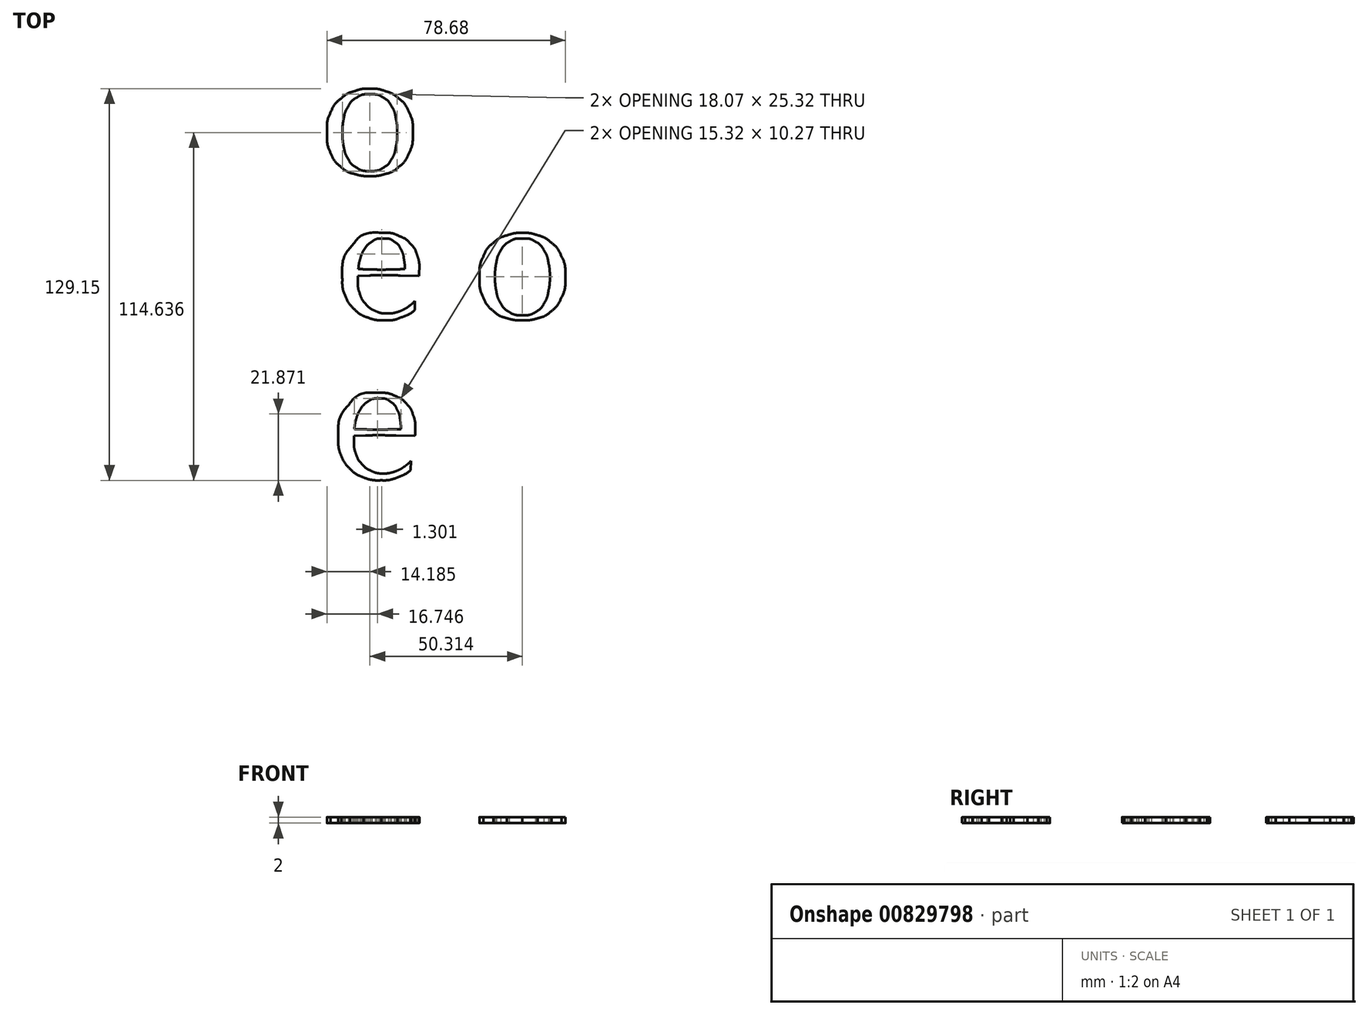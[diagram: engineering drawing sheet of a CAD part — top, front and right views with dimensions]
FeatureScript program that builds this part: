
annotation { "Feature Type Name" : "Feature", "Feature Type Description" : "" }
export const myFeature = defineFeature(function(context is Context, id is Id, definition is map)
    precondition{}
    {
        {
            var Q0;
            Q0=qCreatedBy(makeId("Top.planeOp"),FACE);
            var sketch = newSketch(context, id + "F0", { "sketchPlane" : qUnion([Q0])});
            skLineSegment(sketch, "E0", {"start": v(-57.99, 57.84) * mm, "end": v(-57.99, 47.83) * mm});
            skLineSegment(sketch, "E1", {"start": v(-57.99, 47.83) * mm, "end": v(-57.99, 57.84) * mm});
            skLineSegment(sketch, "E2", {"start": v(-53.21, 47.83) * mm, "end": v(-53.21, 57.84) * mm});
            skLineSegment(sketch, "E3", {"start": v(-53.21, 57.84) * mm, "end": v(-53.21, 47.83) * mm});
            skLineSegment(sketch, "E4", {"start": v(31.74, 55.8) * mm, "end": v(32.14, 56.1) * mm});
            skLineSegment(sketch, "E5", {"start": v(32.14, 56.1) * mm, "end": v(31.74, 55.8) * mm});
            skLineSegment(sketch, "E6", {"start": v(23, 54.88) * mm, "end": v(22.89, 54.93) * mm});
            skLineSegment(sketch, "E7", {"start": v(22.89, 54.93) * mm, "end": v(23, 54.88) * mm});
            skLineSegment(sketch, "E8", {"start": v(18.64, 48.53) * mm, "end": v(18.64, 46.67) * mm});
            skLineSegment(sketch, "E9", {"start": v(18.64, 46.67) * mm, "end": v(18.64, 48.53) * mm});
            skLineSegment(sketch, "E10", {"start": v(22.94, 42.24) * mm, "end": v(22.94, 48.65) * mm});
            skLineSegment(sketch, "E11", {"start": v(22.94, 48.65) * mm, "end": v(22.94, 42.24) * mm});
            skLineSegment(sketch, "E12", {"start": v(56.83, 49.29) * mm, "end": v(56.83, 45.73) * mm});
            skLineSegment(sketch, "E13", {"start": v(56.83, 45.73) * mm, "end": v(56.83, 49.29) * mm});
            skLineSegment(sketch, "E14", {"start": v(61.14, 36.48) * mm, "end": v(61.14, 40.26) * mm});
            skLineSegment(sketch, "E15", {"start": v(61.14, 40.26) * mm, "end": v(61.14, 36.48) * mm});
            skLineSegment(sketch, "E16", {"start": v(42.74, 55.92) * mm, "end": v(42.62, 55.92) * mm});
            skLineSegment(sketch, "E17", {"start": v(42.62, 55.92) * mm, "end": v(42.74, 55.92) * mm});
            skLineSegment(sketch, "E18", {"start": v(38.31, 49.7) * mm, "end": v(38.31, 43.64) * mm});
            skLineSegment(sketch, "E19", {"start": v(38.31, 43.64) * mm, "end": v(38.31, 49.7) * mm});
            skLineSegment(sketch, "E20", {"start": v(42.62, 43.64) * mm, "end": v(42.62, 48.59) * mm});
            skLineSegment(sketch, "E21", {"start": v(42.62, 48.59) * mm, "end": v(42.62, 43.64) * mm});
            skLineSegment(sketch, "E22", {"start": v(-57.28, 2.15) * mm, "end": v(-57.28, -3.9) * mm});
            skLineSegment(sketch, "E23", {"start": v(-57.28, -3.9) * mm, "end": v(-57.28, 2.15) * mm});
            skLineSegment(sketch, "E24", {"start": v(-52.97, -3.9) * mm, "end": v(-52.97, 1.05) * mm});
            skLineSegment(sketch, "E25", {"start": v(-52.97, 1.05) * mm, "end": v(-52.97, -3.9) * mm});
            skLineSegment(sketch, "E26", {"start": v(-35.62, 7.86) * mm, "end": v(-35.74, 7.86) * mm});
            skLineSegment(sketch, "E27", {"start": v(-35.74, 7.86) * mm, "end": v(-35.62, 7.86) * mm});
            skLineSegment(sketch, "E28", {"start": v(-52.86, 8.38) * mm, "end": v(-52.97, 8.38) * mm});
            skLineSegment(sketch, "E29", {"start": v(-52.97, 8.38) * mm, "end": v(-52.86, 8.38) * mm});
            skLineSegment(sketch, "E30", {"start": v(12.53, -11.82) * mm, "end": v(12.88, -8.97) * mm});
            skLineSegment(sketch, "E31", {"start": v(12.88, -8.97) * mm, "end": v(12.59, -8.8) * mm});
            skLineSegment(sketch, "E32", {"start": v(12.59, -8.8) * mm, "end": v(12.53, -11.82) * mm});
            skLineSegment(sketch, "E33", {"start": v(-6.22, -2.16) * mm, "end": v(-6.22, -1.4) * mm});
            skLineSegment(sketch, "E34", {"start": v(-6.22, -1.4) * mm, "end": v(-6.22, -2.16) * mm});
            skLineSegment(sketch, "E35", {"start": v(25.05, 20.84) * mm, "end": v(20.22, 18.8) * mm});
            skLineSegment(sketch, "E36", {"start": v(20.22, 18.8) * mm, "end": v(25.05, 20.84) * mm});
            skLineSegment(sketch, "E37", {"start": v(18.7, 10.07) * mm, "end": v(20.57, 10.07) * mm});
            skLineSegment(sketch, "E38", {"start": v(20.57, 10.07) * mm, "end": v(18.7, 10.07) * mm});
            skLineSegment(sketch, "E39", {"start": v(31.8, -14.5) * mm, "end": v(31.8, -13.1) * mm});
            skLineSegment(sketch, "E40", {"start": v(31.8, -13.1) * mm, "end": v(31.8, -14.5) * mm});
            skLineSegment(sketch, "E41", {"start": v(24.88, 10.07) * mm, "end": v(27.73, 10.07) * mm});
            skLineSegment(sketch, "E42", {"start": v(27.73, 10.07) * mm, "end": v(24.88, 10.07) * mm});
            skLineSegment(sketch, "E43", {"start": v(31, 10.54) * mm, "end": v(31, 11.18) * mm});
            skLineSegment(sketch, "E44", {"start": v(31, 11.18) * mm, "end": v(31, 11.76) * mm});
            skLineSegment(sketch, "E45", {"start": v(31, 11.76) * mm, "end": v(31, 10.54) * mm});
            skLineSegment(sketch, "E46", {"start": v(25.34, 20.84) * mm, "end": v(25.05, 20.84) * mm});
            skLineSegment(sketch, "E47", {"start": v(25.05, 20.84) * mm, "end": v(25.34, 20.84) * mm});
            skLineSegment(sketch, "E48", {"start": v(-22.75, -61.83) * mm, "end": v(-22.93, -67.36) * mm});
            skLineSegment(sketch, "E49", {"start": v(-22.93, -67.36) * mm, "end": v(-22.75, -61.83) * mm});
            skLineSegment(sketch, "E50", {"start": v(-22.93, -39.24) * mm, "end": v(-22.93, -44.95) * mm});
            skLineSegment(sketch, "E51", {"start": v(-22.93, -44.95) * mm, "end": v(-23.05, -44.95) * mm});
            skLineSegment(sketch, "E52", {"start": v(-23.05, -44.95) * mm, "end": v(-22.93, -39.24) * mm});
            skLineSegment(sketch, "E53", {"start": v(-22.87, -61.83) * mm, "end": v(-22.75, -61.83) * mm});
            skLineSegment(sketch, "E54", {"start": v(-22.75, -61.83) * mm, "end": v(-22.87, -61.83) * mm});
            skLineSegment(sketch, "E55", {"start": v(11.23, -64.57) * mm, "end": v(11.58, -61.72) * mm});
            skLineSegment(sketch, "E56", {"start": v(11.58, -61.72) * mm, "end": v(11.29, -61.54) * mm});
            skLineSegment(sketch, "E57", {"start": v(11.29, -61.54) * mm, "end": v(11.23, -64.57) * mm});
            skLineSegment(sketch, "E58", {"start": v(-7.52, -54.9) * mm, "end": v(-7.52, -54.15) * mm});
            skLineSegment(sketch, "E59", {"start": v(-7.52, -54.15) * mm, "end": v(-7.52, -54.9) * mm});
            skLineSegment(sketch, "E60", {"start": v(37.72, -51) * mm, "end": v(37.72, -54.55) * mm});
            skLineSegment(sketch, "E61", {"start": v(37.72, -54.55) * mm, "end": v(37.72, -51) * mm});
            skLineSegment(sketch, "E62", {"start": v(42.03, -63.81) * mm, "end": v(42.03, -60.03) * mm});
            skLineSegment(sketch, "E63", {"start": v(42.03, -60.03) * mm, "end": v(42.03, -63.81) * mm});
            skLineSegment(sketch, "E64", {"start": v(23.63, -44.36) * mm, "end": v(23.52, -44.36) * mm});
            skLineSegment(sketch, "E65", {"start": v(23.52, -44.36) * mm, "end": v(23.63, -44.36) * mm});
            skLineSegment(sketch, "E66", {"start": v(19.2, -50.6) * mm, "end": v(19.2, -56.65) * mm});
            skLineSegment(sketch, "E67", {"start": v(19.2, -56.65) * mm, "end": v(19.2, -50.6) * mm});
            skLineSegment(sketch, "E68", {"start": v(23.52, -56.65) * mm, "end": v(23.52, -51.7) * mm});
            skLineSegment(sketch, "E69", {"start": v(23.52, -51.7) * mm, "end": v(23.52, -56.65) * mm});
            skFitSpline(sketch, "E70", {"points": [v(-57.99, 47.83) * mm, v(-57.99, 45.27) * mm, v(-58.04, 42.75) * mm, v(-58.16, 40.26) * mm]});
            skFitSpline(sketch, "E71", {"points": [v(-58.16, 40.26) * mm, v(-58.24, 37.78) * mm, v(-58.34, 35.33) * mm, v(-58.45, 32.92) * mm]});
            skFitSpline(sketch, "E72", {"points": [v(-58.45, 32.92) * mm, v(-57.13, 33) * mm, v(-55.83, 33.04) * mm, v(-54.55, 33.04) * mm]});
            skFitSpline(sketch, "E73", {"points": [v(-54.55, 33.04) * mm, v(-53.27, 33.04) * mm, v(-51.97, 33.04) * mm, v(-50.65, 33.04) * mm]});
            skFitSpline(sketch, "E74", {"points": [v(-50.65, 33.04) * mm, v(-49.33, 33.04) * mm, v(-48.03, 33.02) * mm, v(-46.75, 32.98) * mm]});
            skFitSpline(sketch, "E75", {"points": [v(-46.75, 32.98) * mm, v(-45.47, 32.94) * mm, v(-44.17, 32.92) * mm, v(-42.85, 32.92) * mm]});
            skFitSpline(sketch, "E76", {"points": [v(-42.85, 32.92) * mm, v(-40.56, 32.92) * mm, v(-38.17, 33.25) * mm, v(-35.69, 33.91) * mm]});
            skFitSpline(sketch, "E77", {"points": [v(-35.69, 33.91) * mm, v(-33.16, 34.61) * mm, v(-30.87, 35.78) * mm, v(-28.82, 37.4) * mm]});
            skFitSpline(sketch, "E78", {"points": [v(-28.82, 37.4) * mm, v(-26.72, 39.04) * mm, v(-25.01, 41.17) * mm, v(-23.7, 43.81) * mm]});
            skFitSpline(sketch, "E79", {"points": [v(-23.7, 43.81) * mm, v(-22.33, 46.5) * mm, v(-21.65, 49.77) * mm, v(-21.65, 53.65) * mm]});
            skFitSpline(sketch, "E80", {"points": [v(-21.65, 53.65) * mm, v(-21.65, 56.64) * mm, v(-22.02, 59.32) * mm, v(-22.76, 61.69) * mm]});
            skFitSpline(sketch, "E81", {"points": [v(-22.76, 61.69) * mm, v(-23.46, 64.1) * mm, v(-24.58, 66.11) * mm, v(-26.14, 67.74) * mm]});
            skFitSpline(sketch, "E82", {"points": [v(-26.14, 67.74) * mm, v(-27.7, 69.41) * mm, v(-29.69, 70.7) * mm, v(-32.13, 71.59) * mm]});
            skFitSpline(sketch, "E83", {"points": [v(-32.13, 71.59) * mm, v(-34.54, 72.48) * mm, v(-37.45, 72.92) * mm, v(-40.87, 72.92) * mm]});
            skFitSpline(sketch, "E84", {"points": [v(-40.87, 72.92) * mm, v(-42.34, 72.92) * mm, v(-43.82, 72.87) * mm, v(-45.3, 72.75) * mm]});
            skFitSpline(sketch, "E85", {"points": [v(-45.3, 72.75) * mm, v(-46.73, 72.67) * mm, v(-48.19, 72.63) * mm, v(-49.66, 72.63) * mm]});
            skFitSpline(sketch, "E86", {"points": [v(-49.66, 72.63) * mm, v(-51.14, 72.63) * mm, v(-52.61, 72.65) * mm, v(-54.09, 72.7) * mm]});
            skFitSpline(sketch, "E87", {"points": [v(-54.09, 72.7) * mm, v(-55.52, 72.77) * mm, v(-56.98, 72.85) * mm, v(-58.45, 72.92) * mm]});
            skFitSpline(sketch, "E88", {"points": [v(-58.45, 72.92) * mm, v(-58.34, 70.36) * mm, v(-58.24, 67.84) * mm, v(-58.16, 65.36) * mm]});
            skFitSpline(sketch, "E89", {"points": [v(-58.16, 65.36) * mm, v(-58.04, 62.91) * mm, v(-57.99, 60.4) * mm, v(-57.99, 57.84) * mm]});
            skFitSpline(sketch, "E90", {"points": [v(-53.21, 57.84) * mm, v(-53.21, 59.94) * mm, v(-53.2, 62) * mm, v(-53.15, 64.02) * mm]});
            skFitSpline(sketch, "E91", {"points": [v(-53.15, 64.02) * mm, v(-53.08, 66.07) * mm, v(-52.98, 68.03) * mm, v(-52.86, 69.9) * mm]});
            skFitSpline(sketch, "E92", {"points": [v(-52.86, 69.9) * mm, v(-51.66, 70.05) * mm, v(-50.3, 70.19) * mm, v(-48.79, 70.3) * mm]});
            skFitSpline(sketch, "E93", {"points": [v(-48.79, 70.3) * mm, v(-47.27, 70.42) * mm, v(-45.64, 70.48) * mm, v(-43.9, 70.48) * mm]});
            skFitSpline(sketch, "E94", {"points": [v(-43.9, 70.48) * mm, v(-41.49, 70.48) * mm, v(-39.28, 70.23) * mm, v(-37.26, 69.72) * mm]});
            skFitSpline(sketch, "E95", {"points": [v(-37.26, 69.72) * mm, v(-35.24, 69.26) * mm, v(-33.51, 68.38) * mm, v(-32.08, 67.1) * mm]});
            skFitSpline(sketch, "E96", {"points": [v(-32.08, 67.1) * mm, v(-30.6, 65.86) * mm, v(-29.46, 64.15) * mm, v(-28.64, 61.98) * mm]});
            skFitSpline(sketch, "E97", {"points": [v(-28.64, 61.98) * mm, v(-27.79, 59.8) * mm, v(-27.36, 57.03) * mm, v(-27.36, 53.65) * mm]});
            skFitSpline(sketch, "E98", {"points": [v(-27.36, 53.65) * mm, v(-27.36, 49.8) * mm, v(-27.9, 46.67) * mm, v(-29, 44.22) * mm]});
            skFitSpline(sketch, "E99", {"points": [v(-29, 44.22) * mm, v(-30.04, 41.81) * mm, v(-31.42, 39.91) * mm, v(-33.12, 38.51) * mm]});
            skFitSpline(sketch, "E100", {"points": [v(-33.12, 38.51) * mm, v(-34.8, 37.12) * mm, v(-36.7, 36.17) * mm, v(-38.83, 35.66) * mm]});
            skFitSpline(sketch, "E101", {"points": [v(-38.83, 35.66) * mm, v(-40.97, 35.16) * mm, v(-43.1, 34.9) * mm, v(-45.24, 34.9) * mm]});
            skFitSpline(sketch, "E102", {"points": [v(-45.24, 34.9) * mm, v(-46.71, 34.9) * mm, v(-48.15, 34.94) * mm, v(-49.54, 35.02) * mm]});
            skFitSpline(sketch, "E103", {"points": [v(-49.54, 35.02) * mm, v(-50.94, 35.14) * mm, v(-52.05, 35.3) * mm, v(-52.86, 35.49) * mm]});
            skFitSpline(sketch, "E104", {"points": [v(-52.86, 35.49) * mm, v(-53.1, 39.52) * mm, v(-53.21, 43.64) * mm, v(-53.21, 47.83) * mm]});
            skFitSpline(sketch, "E105", {"points": [v(-11.27, 46.67) * mm, v(-11.27, 48.3) * mm, v(-11.13, 49.87) * mm, v(-10.86, 51.38) * mm]});
            skFitSpline(sketch, "E106", {"points": [v(-10.86, 51.38) * mm, v(-10.55, 52.9) * mm, v(-10.05, 54.23) * mm, v(-9.35, 55.4) * mm]});
            skFitSpline(sketch, "E107", {"points": [v(-9.35, 55.4) * mm, v(-8.65, 56.6) * mm, v(-7.72, 57.55) * mm, v(-6.55, 58.25) * mm]});
            skFitSpline(sketch, "E108", {"points": [v(-6.55, 58.25) * mm, v(-5.39, 58.95) * mm, v(-3.95, 59.3) * mm, v(-2.25, 59.3) * mm]});
            skFitSpline(sketch, "E109", {"points": [v(-2.25, 59.3) * mm, v(-0.54, 59.3) * mm, v(0.9, 58.95) * mm, v(2.06, 58.25) * mm]});
            skFitSpline(sketch, "E110", {"points": [v(2.06, 58.25) * mm, v(3.23, 57.55) * mm, v(4.16, 56.6) * mm, v(4.86, 55.4) * mm]});
            skFitSpline(sketch, "E111", {"points": [v(4.86, 55.4) * mm, v(5.56, 54.23) * mm, v(6.04, 52.9) * mm, v(6.31, 51.38) * mm]});
            skFitSpline(sketch, "E112", {"points": [v(6.31, 51.38) * mm, v(6.62, 49.87) * mm, v(6.78, 48.3) * mm, v(6.78, 46.67) * mm]});
            skFitSpline(sketch, "E113", {"points": [v(6.78, 46.67) * mm, v(6.78, 45.04) * mm, v(6.62, 43.46) * mm, v(6.31, 41.95) * mm]});
            skFitSpline(sketch, "E114", {"points": [v(6.31, 41.95) * mm, v(6.04, 40.44) * mm, v(5.56, 39.08) * mm, v(4.86, 37.87) * mm]});
            skFitSpline(sketch, "E115", {"points": [v(4.86, 37.87) * mm, v(4.16, 36.7) * mm, v(3.23, 35.78) * mm, v(2.06, 35.08) * mm]});
            skFitSpline(sketch, "E116", {"points": [v(2.06, 35.08) * mm, v(0.9, 34.38) * mm, v(-0.54, 34.03) * mm, v(-2.25, 34.03) * mm]});
            skFitSpline(sketch, "E117", {"points": [v(-2.25, 34.03) * mm, v(-3.95, 34.03) * mm, v(-5.39, 34.38) * mm, v(-6.55, 35.08) * mm]});
            skFitSpline(sketch, "E118", {"points": [v(-6.55, 35.08) * mm, v(-7.72, 35.78) * mm, v(-8.65, 36.7) * mm, v(-9.35, 37.87) * mm]});
            skFitSpline(sketch, "E119", {"points": [v(-9.35, 37.87) * mm, v(-10.05, 39.08) * mm, v(-10.55, 40.44) * mm, v(-10.86, 41.95) * mm]});
            skFitSpline(sketch, "E120", {"points": [v(-10.86, 41.95) * mm, v(-11.13, 43.46) * mm, v(-11.27, 45.04) * mm, v(-11.27, 46.67) * mm]});
            skFitSpline(sketch, "E121", {"points": [v(-16.4, 46.67) * mm, v(-16.4, 44.03) * mm, v(-15.99, 41.77) * mm, v(-15.17, 39.91) * mm]});
            skFitSpline(sketch, "E122", {"points": [v(-15.17, 39.91) * mm, v(-14.32, 38.09) * mm, v(-13.21, 36.6) * mm, v(-11.85, 35.43) * mm]});
            skFitSpline(sketch, "E123", {"points": [v(-11.85, 35.43) * mm, v(-10.5, 34.3) * mm, v(-8.98, 33.5) * mm, v(-7.31, 33.04) * mm]});
            skFitSpline(sketch, "E124", {"points": [v(-7.31, 33.04) * mm, v(-5.6, 32.58) * mm, v(-3.91, 32.34) * mm, v(-2.25, 32.34) * mm]});
            skFitSpline(sketch, "E125", {"points": [v(-2.25, 32.34) * mm, v(-0.54, 32.34) * mm, v(1.15, 32.58) * mm, v(2.82, 33.04) * mm]});
            skFitSpline(sketch, "E126", {"points": [v(2.82, 33.04) * mm, v(4.49, 33.5) * mm, v(6, 34.3) * mm, v(7.36, 35.43) * mm]});
            skFitSpline(sketch, "E127", {"points": [v(7.36, 35.43) * mm, v(8.72, 36.6) * mm, v(9.8, 38.09) * mm, v(10.62, 39.91) * mm]});
            skFitSpline(sketch, "E128", {"points": [v(10.62, 39.91) * mm, v(11.48, 41.77) * mm, v(11.9, 44.03) * mm, v(11.9, 46.67) * mm]});
            skFitSpline(sketch, "E129", {"points": [v(11.9, 46.67) * mm, v(11.9, 49.3) * mm, v(11.48, 51.54) * mm, v(10.62, 53.36) * mm]});
            skFitSpline(sketch, "E130", {"points": [v(10.62, 53.36) * mm, v(9.8, 55.22) * mm, v(8.72, 56.72) * mm, v(7.36, 57.84) * mm]});
            skFitSpline(sketch, "E131", {"points": [v(7.36, 57.84) * mm, v(6, 59) * mm, v(4.49, 59.84) * mm, v(2.82, 60.35) * mm]});
            skFitSpline(sketch, "E132", {"points": [v(2.82, 60.35) * mm, v(1.15, 60.9) * mm, v(-0.54, 61.16) * mm, v(-2.25, 61.16) * mm]});
            skFitSpline(sketch, "E133", {"points": [v(-2.25, 61.16) * mm, v(-3.91, 61.16) * mm, v(-5.6, 60.9) * mm, v(-7.31, 60.35) * mm]});
            skFitSpline(sketch, "E134", {"points": [v(-7.31, 60.35) * mm, v(-8.98, 59.84) * mm, v(-10.5, 59) * mm, v(-11.85, 57.84) * mm]});
            skFitSpline(sketch, "E135", {"points": [v(-11.85, 57.84) * mm, v(-13.21, 56.72) * mm, v(-14.32, 55.22) * mm, v(-15.17, 53.36) * mm]});
            skFitSpline(sketch, "E136", {"points": [v(-15.17, 53.36) * mm, v(-15.99, 51.54) * mm, v(-16.4, 49.3) * mm, v(-16.4, 46.67) * mm]});
            skFitSpline(sketch, "E137", {"points": [v(32.14, 56.1) * mm, v(32.14, 56.87) * mm, v(32.16, 57.73) * mm, v(32.2, 58.66) * mm]});
            skFitSpline(sketch, "E138", {"points": [v(32.2, 58.66) * mm, v(32.24, 59.63) * mm, v(32.36, 60.35) * mm, v(32.55, 60.81) * mm]});
            skFitSpline(sketch, "E139", {"points": [v(32.55, 60.81) * mm, v(32.16, 60.97) * mm, v(31.83, 61.07) * mm, v(31.56, 61.1) * mm]});
            skFitSpline(sketch, "E140", {"points": [v(31.56, 61.1) * mm, v(31.33, 61.14) * mm, v(31.04, 61.16) * mm, v(30.69, 61.16) * mm]});
            skFitSpline(sketch, "E141", {"points": [v(30.69, 61.16) * mm, v(27.85, 61.16) * mm, v(25.3, 59.07) * mm, v(23, 54.88) * mm]});
            skFitSpline(sketch, "E142", {"points": [v(22.89, 54.93) * mm, v(22.89, 55.67) * mm, v(22.89, 56.45) * mm, v(22.89, 57.26) * mm]});
            skFitSpline(sketch, "E143", {"points": [v(22.89, 57.26) * mm, v(22.93, 58.08) * mm, v(23.02, 59.18) * mm, v(23.18, 60.58) * mm]});
            skFitSpline(sketch, "E144", {"points": [v(23.18, 60.58) * mm, v(22.75, 60.5) * mm, v(22.34, 60.43) * mm, v(21.95, 60.35) * mm]});
            skFitSpline(sketch, "E145", {"points": [v(21.95, 60.35) * mm, v(21.57, 60.3) * mm, v(21.2, 60.3) * mm, v(20.85, 60.3) * mm]});
            skFitSpline(sketch, "E146", {"points": [v(20.85, 60.3) * mm, v(20.42, 60.3) * mm, v(20.01, 60.3) * mm, v(19.63, 60.35) * mm]});
            skFitSpline(sketch, "E147", {"points": [v(19.63, 60.35) * mm, v(19.24, 60.43) * mm, v(18.83, 60.5) * mm, v(18.4, 60.58) * mm]});
            skFitSpline(sketch, "E148", {"points": [v(18.4, 60.58) * mm, v(18.52, 58.02) * mm, v(18.58, 55.75) * mm, v(18.58, 53.77) * mm]});
            skFitSpline(sketch, "E149", {"points": [v(18.58, 53.77) * mm, v(18.62, 51.79) * mm, v(18.64, 50.04) * mm, v(18.64, 48.53) * mm]});
            skFitSpline(sketch, "E150", {"points": [v(18.64, 46.67) * mm, v(18.64, 43.37) * mm, v(18.62, 40.57) * mm, v(18.58, 38.28) * mm]});
            skFitSpline(sketch, "E151", {"points": [v(18.58, 38.28) * mm, v(18.58, 36.03) * mm, v(18.52, 34.24) * mm, v(18.4, 32.92) * mm]});
            skFitSpline(sketch, "E152", {"points": [v(18.4, 32.92) * mm, v(19.18, 33) * mm, v(20, 33.04) * mm, v(20.85, 33.04) * mm]});
            skFitSpline(sketch, "E153", {"points": [v(20.85, 33.04) * mm, v(21.62, 33.04) * mm, v(22.4, 33) * mm, v(23.18, 32.92) * mm]});
            skFitSpline(sketch, "E154", {"points": [v(23.18, 32.92) * mm, v(23.06, 33.78) * mm, v(22.98, 34.88) * mm, v(22.94, 36.24) * mm]});
            skFitSpline(sketch, "E155", {"points": [v(22.94, 36.24) * mm, v(22.94, 37.64) * mm, v(22.94, 39.64) * mm, v(22.94, 42.24) * mm]});
            skFitSpline(sketch, "E156", {"points": [v(22.94, 48.65) * mm, v(22.94, 49.77) * mm, v(23.08, 50.82) * mm, v(23.35, 51.79) * mm]});
            skFitSpline(sketch, "E157", {"points": [v(23.35, 51.79) * mm, v(23.62, 52.8) * mm, v(24.01, 53.65) * mm, v(24.52, 54.35) * mm]});
            skFitSpline(sketch, "E158", {"points": [v(24.52, 54.35) * mm, v(25.02, 55.09) * mm, v(25.64, 55.67) * mm, v(26.38, 56.1) * mm]});
            skFitSpline(sketch, "E159", {"points": [v(26.38, 56.1) * mm, v(27.12, 56.52) * mm, v(27.95, 56.74) * mm, v(28.88, 56.74) * mm]});
            skFitSpline(sketch, "E160", {"points": [v(28.88, 56.74) * mm, v(29.47, 56.74) * mm, v(30.03, 56.64) * mm, v(30.57, 56.45) * mm]});
            skFitSpline(sketch, "E161", {"points": [v(30.57, 56.45) * mm, v(31.15, 56.25) * mm, v(31.54, 56.04) * mm, v(31.74, 55.8) * mm]});
            skFitSpline(sketch, "E162", {"points": [v(56.83, 45.73) * mm, v(56.83, 43.48) * mm, v(56.77, 41.29) * mm, v(56.66, 39.15) * mm]});
            skFitSpline(sketch, "E163", {"points": [v(56.66, 39.15) * mm, v(56.58, 37.02) * mm, v(56.5, 34.94) * mm, v(56.42, 32.92) * mm]});
            skFitSpline(sketch, "E164", {"points": [v(56.42, 32.92) * mm, v(57.2, 33) * mm, v(58, 33.04) * mm, v(58.8, 33.04) * mm]});
            skFitSpline(sketch, "E165", {"points": [v(58.8, 33.04) * mm, v(59.66, 33.04) * mm, v(60.48, 33) * mm, v(61.26, 32.92) * mm]});
            skFitSpline(sketch, "E166", {"points": [v(61.26, 32.92) * mm, v(61.22, 33.47) * mm, v(61.18, 34.03) * mm, v(61.14, 34.61) * mm]});
            skFitSpline(sketch, "E167", {"points": [v(61.14, 34.61) * mm, v(61.14, 35.23) * mm, v(61.14, 35.86) * mm, v(61.14, 36.48) * mm]});
            skFitSpline(sketch, "E168", {"points": [v(61.14, 40.26) * mm, v(61.14, 42.24) * mm, v(61.18, 44.1) * mm, v(61.26, 45.85) * mm]});
            skFitSpline(sketch, "E169", {"points": [v(61.26, 45.85) * mm, v(61.33, 47.64) * mm, v(61.37, 49.36) * mm, v(61.37, 51.03) * mm]});
            skFitSpline(sketch, "E170", {"points": [v(61.37, 51.03) * mm, v(61.37, 53.05) * mm, v(61.08, 54.7) * mm, v(60.5, 55.98) * mm]});
            skFitSpline(sketch, "E171", {"points": [v(60.5, 55.98) * mm, v(59.95, 57.3) * mm, v(59.24, 58.33) * mm, v(58.34, 59.07) * mm]});
            skFitSpline(sketch, "E172", {"points": [v(58.34, 59.07) * mm, v(57.45, 59.84) * mm, v(56.44, 60.39) * mm, v(55.32, 60.7) * mm]});
            skFitSpline(sketch, "E173", {"points": [v(55.32, 60.7) * mm, v(54.23, 61) * mm, v(53.14, 61.16) * mm, v(52.06, 61.16) * mm]});
            skFitSpline(sketch, "E174", {"points": [v(52.06, 61.16) * mm, v(49.96, 61.16) * mm, v(48.15, 60.7) * mm, v(46.64, 59.77) * mm]});
            skFitSpline(sketch, "E175", {"points": [v(46.64, 59.77) * mm, v(45.13, 58.87) * mm, v(43.83, 57.6) * mm, v(42.74, 55.92) * mm]});
            skFitSpline(sketch, "E176", {"points": [v(42.62, 55.92) * mm, v(42.62, 57.48) * mm, v(42.68, 59.03) * mm, v(42.8, 60.58) * mm]});
            skFitSpline(sketch, "E177", {"points": [v(42.8, 60.58) * mm, v(42.3, 60.5) * mm, v(41.85, 60.43) * mm, v(41.46, 60.35) * mm]});
            skFitSpline(sketch, "E178", {"points": [v(41.46, 60.35) * mm, v(41.1, 60.3) * mm, v(40.78, 60.3) * mm, v(40.47, 60.3) * mm]});
            skFitSpline(sketch, "E179", {"points": [v(40.47, 60.3) * mm, v(39.8, 60.3) * mm, v(38.94, 60.39) * mm, v(37.85, 60.58) * mm]});
            skFitSpline(sketch, "E180", {"points": [v(37.85, 60.58) * mm, v(38.04, 58.91) * mm, v(38.16, 57.1) * mm, v(38.2, 55.17) * mm]});
            skFitSpline(sketch, "E181", {"points": [v(38.2, 55.17) * mm, v(38.28, 53.26) * mm, v(38.31, 51.44) * mm, v(38.31, 49.7) * mm]});
            skFitSpline(sketch, "E182", {"points": [v(38.31, 43.64) * mm, v(38.31, 41.9) * mm, v(38.28, 40.05) * mm, v(38.2, 38.1) * mm]});
            skFitSpline(sketch, "E183", {"points": [v(38.2, 38.1) * mm, v(38.16, 36.2) * mm, v(38.04, 34.48) * mm, v(37.85, 32.92) * mm]});
            skFitSpline(sketch, "E184", {"points": [v(37.85, 32.92) * mm, v(38.74, 33) * mm, v(39.62, 33.04) * mm, v(40.47, 33.04) * mm]});
            skFitSpline(sketch, "E185", {"points": [v(40.47, 33.04) * mm, v(41.32, 33.04) * mm, v(42.2, 33) * mm, v(43.09, 32.92) * mm]});
            skFitSpline(sketch, "E186", {"points": [v(43.09, 32.92) * mm, v(42.9, 34.48) * mm, v(42.76, 36.2) * mm, v(42.68, 38.1) * mm]});
            skFitSpline(sketch, "E187", {"points": [v(42.68, 38.1) * mm, v(42.64, 40.05) * mm, v(42.62, 41.9) * mm, v(42.62, 43.64) * mm]});
            skFitSpline(sketch, "E188", {"points": [v(42.62, 48.59) * mm, v(42.62, 51.61) * mm, v(43.24, 53.96) * mm, v(44.49, 55.63) * mm]});
            skFitSpline(sketch, "E189", {"points": [v(44.49, 55.63) * mm, v(45.77, 57.3) * mm, v(47.77, 58.14) * mm, v(50.48, 58.14) * mm]});
            skFitSpline(sketch, "E190", {"points": [v(50.48, 58.14) * mm, v(52.46, 58.14) * mm, v(54.02, 57.38) * mm, v(55.14, 55.87) * mm]});
            skFitSpline(sketch, "E191", {"points": [v(55.14, 55.87) * mm, v(56.27, 54.4) * mm, v(56.83, 52.2) * mm, v(56.83, 49.29) * mm]});
            skFitSpline(sketch, "E192", {"points": [v(-57.28, -3.9) * mm, v(-57.28, -5.65) * mm, v(-57.32, -7.5) * mm, v(-57.4, -9.43) * mm]});
            skFitSpline(sketch, "E193", {"points": [v(-57.4, -9.43) * mm, v(-57.44, -11.34) * mm, v(-57.55, -13.06) * mm, v(-57.75, -14.62) * mm]});
            skFitSpline(sketch, "E194", {"points": [v(-57.75, -14.62) * mm, v(-56.85, -14.54) * mm, v(-55.98, -14.5) * mm, v(-55.13, -14.5) * mm]});
            skFitSpline(sketch, "E195", {"points": [v(-55.13, -14.5) * mm, v(-54.27, -14.5) * mm, v(-53.4, -14.54) * mm, v(-52.5, -14.62) * mm]});
            skFitSpline(sketch, "E196", {"points": [v(-52.5, -14.62) * mm, v(-52.7, -13.06) * mm, v(-52.84, -11.34) * mm, v(-52.91, -9.43) * mm]});
            skFitSpline(sketch, "E197", {"points": [v(-52.91, -9.43) * mm, v(-52.95, -7.5) * mm, v(-52.97, -5.65) * mm, v(-52.97, -3.9) * mm]});
            skFitSpline(sketch, "E198", {"points": [v(-52.97, 1.05) * mm, v(-52.97, 4.07) * mm, v(-52.37, 6.42) * mm, v(-51.17, 8.1) * mm]});
            skFitSpline(sketch, "E199", {"points": [v(-51.17, 8.1) * mm, v(-49.96, 9.76) * mm, v(-48.08, 10.6) * mm, v(-45.52, 10.6) * mm]});
            skFitSpline(sketch, "E200", {"points": [v(-45.52, 10.6) * mm, v(-44.55, 10.6) * mm, v(-43.62, 10.32) * mm, v(-42.73, 9.78) * mm]});
            skFitSpline(sketch, "E201", {"points": [v(-42.73, 9.78) * mm, v(-41.8, 9.28) * mm, v(-41.11, 8.65) * mm, v(-40.69, 7.92) * mm]});
            skFitSpline(sketch, "E202", {"points": [v(-40.69, 7.92) * mm, v(-40.45, 7.45) * mm, v(-40.28, 7.02) * mm, v(-40.16, 6.64) * mm]});
            skFitSpline(sketch, "E203", {"points": [v(-40.16, 6.64) * mm, v(-40, 6.25) * mm, v(-39.9, 5.74) * mm, v(-39.81, 5.12) * mm]});
            skFitSpline(sketch, "E204", {"points": [v(-39.81, 5.12) * mm, v(-39.74, 4.54) * mm, v(-39.7, 3.72) * mm, v(-39.7, 2.68) * mm]});
            skFitSpline(sketch, "E205", {"points": [v(-39.7, 2.68) * mm, v(-39.66, 1.67) * mm, v(-39.64, 0.25) * mm, v(-39.64, -1.57) * mm]});
            skFitSpline(sketch, "E206", {"points": [v(-39.64, -1.57) * mm, v(-39.64, -3.7) * mm, v(-39.68, -5.88) * mm, v(-39.76, -8.1) * mm]});
            skFitSpline(sketch, "E207", {"points": [v(-39.76, -8.1) * mm, v(-39.83, -10.3) * mm, v(-39.97, -12.48) * mm, v(-40.16, -14.62) * mm]});
            skFitSpline(sketch, "E208", {"points": [v(-40.16, -14.62) * mm, v(-39.27, -14.54) * mm, v(-38.42, -14.5) * mm, v(-37.6, -14.5) * mm]});
            skFitSpline(sketch, "E209", {"points": [v(-37.6, -14.5) * mm, v(-36.79, -14.5) * mm, v(-35.93, -14.54) * mm, v(-35.04, -14.62) * mm]});
            skFitSpline(sketch, "E210", {"points": [v(-35.04, -14.62) * mm, v(-35.12, -12.99) * mm, v(-35.2, -11.5) * mm, v(-35.27, -10.13) * mm]});
            skFitSpline(sketch, "E211", {"points": [v(-35.27, -10.13) * mm, v(-35.31, -8.74) * mm, v(-35.33, -7.2) * mm, v(-35.33, -5.53) * mm]});
            skFitSpline(sketch, "E212", {"points": [v(-35.33, -5.53) * mm, v(-35.33, -2.78) * mm, v(-35.31, -0.62) * mm, v(-35.27, 0.93) * mm]});
            skFitSpline(sketch, "E213", {"points": [v(-35.27, 0.93) * mm, v(-35.23, 2.52) * mm, v(-35.18, 3.74) * mm, v(-35.1, 4.6) * mm]});
            skFitSpline(sketch, "E214", {"points": [v(-35.1, 4.6) * mm, v(-34.98, 5.5) * mm, v(-34.85, 6.15) * mm, v(-34.7, 6.58) * mm]});
            skFitSpline(sketch, "E215", {"points": [v(-34.7, 6.58) * mm, v(-34.5, 7) * mm, v(-34.24, 7.43) * mm, v(-33.93, 7.86) * mm]});
            skFitSpline(sketch, "E216", {"points": [v(-33.93, 7.86) * mm, v(-33.39, 8.6) * mm, v(-32.63, 9.24) * mm, v(-31.66, 9.78) * mm]});
            skFitSpline(sketch, "E217", {"points": [v(-31.66, 9.78) * mm, v(-30.7, 10.32) * mm, v(-29.5, 10.6) * mm, v(-28.11, 10.6) * mm]});
            skFitSpline(sketch, "E218", {"points": [v(-28.11, 10.6) * mm, v(-26.95, 10.6) * mm, v(-25.98, 10.4) * mm, v(-25.2, 10.01) * mm]});
            skFitSpline(sketch, "E219", {"points": [v(-25.2, 10.01) * mm, v(-24.42, 9.66) * mm, v(-23.8, 9.18) * mm, v(-23.34, 8.56) * mm]});
            skFitSpline(sketch, "E220", {"points": [v(-23.34, 8.56) * mm, v(-22.87, 7.94) * mm, v(-22.54, 7.2) * mm, v(-22.35, 6.34) * mm]});
            skFitSpline(sketch, "E221", {"points": [v(-22.35, 6.34) * mm, v(-22.11, 5.5) * mm, v(-22, 4.58) * mm, v(-22, 3.6) * mm]});
            skFitSpline(sketch, "E222", {"points": [v(-22, 3.6) * mm, v(-22, -1.67) * mm, v(-22.07, -5.79) * mm, v(-22.23, -8.74) * mm]});
            skFitSpline(sketch, "E223", {"points": [v(-22.23, -8.74) * mm, v(-22.35, -11.69) * mm, v(-22.46, -13.65) * mm, v(-22.58, -14.62) * mm]});
            skFitSpline(sketch, "E224", {"points": [v(-22.58, -14.62) * mm, v(-22.15, -14.54) * mm, v(-21.73, -14.5) * mm, v(-21.3, -14.5) * mm]});
            skFitSpline(sketch, "E225", {"points": [v(-21.3, -14.5) * mm, v(-20.87, -14.5) * mm, v(-20.44, -14.5) * mm, v(-20.02, -14.5) * mm]});
            skFitSpline(sketch, "E226", {"points": [v(-20.02, -14.5) * mm, v(-19.63, -14.5) * mm, v(-19.22, -14.5) * mm, v(-18.8, -14.5) * mm]});
            skFitSpline(sketch, "E227", {"points": [v(-18.8, -14.5) * mm, v(-18.37, -14.5) * mm, v(-17.94, -14.54) * mm, v(-17.51, -14.62) * mm]});
            skFitSpline(sketch, "E228", {"points": [v(-17.51, -14.62) * mm, v(-17.6, -13.5) * mm, v(-17.65, -12.44) * mm, v(-17.69, -11.47) * mm]});
            skFitSpline(sketch, "E229", {"points": [v(-17.69, -11.47) * mm, v(-17.69, -10.5) * mm, v(-17.69, -9.5) * mm, v(-17.69, -8.44) * mm]});
            skFitSpline(sketch, "E230", {"points": [v(-17.69, -8.44) * mm, v(-17.69, -6.74) * mm, v(-17.67, -5.24) * mm, v(-17.63, -3.96) * mm]});
            skFitSpline(sketch, "E231", {"points": [v(-17.63, -3.96) * mm, v(-17.6, -2.64) * mm, v(-17.55, -1.48) * mm, v(-17.51, -0.47) * mm]});
            skFitSpline(sketch, "E232", {"points": [v(-17.51, -0.47) * mm, v(-17.48, 0.58) * mm, v(-17.44, 1.5) * mm, v(-17.4, 2.27) * mm]});
            skFitSpline(sketch, "E233", {"points": [v(-17.4, 2.27) * mm, v(-17.36, 3.05) * mm, v(-17.34, 3.76) * mm, v(-17.34, 4.42) * mm]});
            skFitSpline(sketch, "E234", {"points": [v(-17.34, 4.42) * mm, v(-17.34, 6.05) * mm, v(-17.57, 7.45) * mm, v(-18.04, 8.62) * mm]});
            skFitSpline(sketch, "E235", {"points": [v(-18.04, 8.62) * mm, v(-18.47, 9.78) * mm, v(-19.09, 10.73) * mm, v(-19.9, 11.47) * mm]});
            skFitSpline(sketch, "E236", {"points": [v(-19.9, 11.47) * mm, v(-20.68, 12.2) * mm, v(-21.6, 12.75) * mm, v(-22.7, 13.1) * mm]});
            skFitSpline(sketch, "E237", {"points": [v(-22.7, 13.1) * mm, v(-23.78, 13.45) * mm, v(-24.97, 13.62) * mm, v(-26.25, 13.62) * mm]});
            skFitSpline(sketch, "E238", {"points": [v(-26.25, 13.62) * mm, v(-28.34, 13.62) * mm, v(-30.2, 13.12) * mm, v(-31.84, 12.1) * mm]});
            skFitSpline(sketch, "E239", {"points": [v(-31.84, 12.1) * mm, v(-33.43, 11.14) * mm, v(-34.7, 9.72) * mm, v(-35.62, 7.86) * mm]});
            skFitSpline(sketch, "E240", {"points": [v(-35.74, 7.86) * mm, v(-35.93, 8.67) * mm, v(-36.3, 9.43) * mm, v(-36.84, 10.13) * mm]});
            skFitSpline(sketch, "E241", {"points": [v(-36.84, 10.13) * mm, v(-37.39, 10.87) * mm, v(-38.05, 11.49) * mm, v(-38.82, 12) * mm]});
            skFitSpline(sketch, "E242", {"points": [v(-38.82, 12) * mm, v(-39.56, 12.5) * mm, v(-40.4, 12.88) * mm, v(-41.33, 13.16) * mm]});
            skFitSpline(sketch, "E243", {"points": [v(-41.33, 13.16) * mm, v(-42.26, 13.47) * mm, v(-43.21, 13.62) * mm, v(-44.18, 13.62) * mm]});
            skFitSpline(sketch, "E244", {"points": [v(-44.18, 13.62) * mm, v(-47.9, 13.62) * mm, v(-50.8, 11.88) * mm, v(-52.86, 8.38) * mm]});
            skFitSpline(sketch, "E245", {"points": [v(-52.97, 8.38) * mm, v(-52.97, 9.93) * mm, v(-52.91, 11.49) * mm, v(-52.8, 13.04) * mm]});
            skFitSpline(sketch, "E246", {"points": [v(-52.8, 13.04) * mm, v(-53.3, 12.96) * mm, v(-53.75, 12.88) * mm, v(-54.14, 12.8) * mm]});
            skFitSpline(sketch, "E247", {"points": [v(-54.14, 12.8) * mm, v(-54.49, 12.77) * mm, v(-54.82, 12.75) * mm, v(-55.13, 12.75) * mm]});
            skFitSpline(sketch, "E248", {"points": [v(-55.13, 12.75) * mm, v(-55.79, 12.75) * mm, v(-56.66, 12.85) * mm, v(-57.75, 13.04) * mm]});
            skFitSpline(sketch, "E249", {"points": [v(-57.75, 13.04) * mm, v(-57.55, 11.37) * mm, v(-57.44, 9.57) * mm, v(-57.4, 7.63) * mm]});
            skFitSpline(sketch, "E250", {"points": [v(-57.4, 7.63) * mm, v(-57.32, 5.72) * mm, v(-57.28, 3.9) * mm, v(-57.28, 2.15) * mm]});
            skFitSpline(sketch, "E251", {"points": [v(2.1, 11.76) * mm, v(3.62, 11.76) * mm, v(4.85, 11.43) * mm, v(5.78, 10.77) * mm]});
            skFitSpline(sketch, "E252", {"points": [v(5.78, 10.77) * mm, v(6.7, 10.1) * mm, v(7.43, 9.28) * mm, v(7.93, 8.27) * mm]});
            skFitSpline(sketch, "E253", {"points": [v(7.93, 8.27) * mm, v(8.48, 7.26) * mm, v(8.82, 6.17) * mm, v(8.98, 5) * mm]});
            skFitSpline(sketch, "E254", {"points": [v(8.98, 5) * mm, v(9.17, 3.84) * mm, v(9.27, 2.73) * mm, v(9.27, 1.69) * mm]});
            skFitSpline(sketch, "E255", {"points": [v(9.27, 1.69) * mm, v(8.03, 1.65) * mm, v(6.75, 1.6) * mm, v(5.43, 1.57) * mm]});
            skFitSpline(sketch, "E256", {"points": [v(5.43, 1.57) * mm, v(4.1, 1.53) * mm, v(2.8, 1.51) * mm, v(1.53, 1.51) * mm]});
            skFitSpline(sketch, "E257", {"points": [v(1.53, 1.51) * mm, v(0.28, 1.51) * mm, v(-1, 1.53) * mm, v(-2.32, 1.57) * mm]});
            skFitSpline(sketch, "E258", {"points": [v(-2.32, 1.57) * mm, v(-3.6, 1.6) * mm, v(-4.84, 1.65) * mm, v(-6.04, 1.69) * mm]});
            skFitSpline(sketch, "E259", {"points": [v(-6.04, 1.69) * mm, v(-5.96, 2.73) * mm, v(-5.77, 3.84) * mm, v(-5.46, 5) * mm]});
            skFitSpline(sketch, "E260", {"points": [v(-5.46, 5) * mm, v(-5.11, 6.2) * mm, v(-4.63, 7.3) * mm, v(-4, 8.27) * mm]});
            skFitSpline(sketch, "E261", {"points": [v(-4, 8.27) * mm, v(-3.34, 9.28) * mm, v(-2.53, 10.1) * mm, v(-1.56, 10.77) * mm]});
            skFitSpline(sketch, "E262", {"points": [v(-1.56, 10.77) * mm, v(-0.55, 11.43) * mm, v(0.67, 11.76) * mm, v(2.1, 11.76) * mm]});
            skFitSpline(sketch, "E263", {"points": [v(-11.34, -1.7) * mm, v(-11.34, -3.63) * mm, v(-11.01, -5.44) * mm, v(-10.35, -7.1) * mm]});
            skFitSpline(sketch, "E264", {"points": [v(-10.35, -7.1) * mm, v(-9.65, -8.77) * mm, v(-8.68, -10.23) * mm, v(-7.44, -11.47) * mm]});
            skFitSpline(sketch, "E265", {"points": [v(-7.44, -11.47) * mm, v(-6.16, -12.68) * mm, v(-4.66, -13.6) * mm, v(-2.96, -14.27) * mm]});
            skFitSpline(sketch, "E266", {"points": [v(-2.96, -14.27) * mm, v(-1.2, -14.89) * mm, v(0.71, -15.2) * mm, v(2.8, -15.2) * mm]});
            skFitSpline(sketch, "E267", {"points": [v(2.8, -15.2) * mm, v(4.67, -15.2) * mm, v(6.46, -14.87) * mm, v(8.16, -14.2) * mm]});
            skFitSpline(sketch, "E268", {"points": [v(8.16, -14.2) * mm, v(9.91, -13.55) * mm, v(11.37, -12.75) * mm, v(12.53, -11.82) * mm]});
            skFitSpline(sketch, "E269", {"points": [v(12.59, -8.8) * mm, v(12.09, -9.38) * mm, v(11.48, -9.92) * mm, v(10.78, -10.42) * mm]});
            skFitSpline(sketch, "E270", {"points": [v(10.78, -10.42) * mm, v(10.12, -10.93) * mm, v(9.4, -11.38) * mm, v(8.63, -11.76) * mm]});
            skFitSpline(sketch, "E271", {"points": [v(8.63, -11.76) * mm, v(7.85, -12.11) * mm, v(7.06, -12.4) * mm, v(6.24, -12.64) * mm]});
            skFitSpline(sketch, "E272", {"points": [v(6.24, -12.64) * mm, v(5.43, -12.83) * mm, v(4.63, -12.93) * mm, v(3.86, -12.93) * mm]});
            skFitSpline(sketch, "E273", {"points": [v(3.86, -12.93) * mm, v(2.23, -12.93) * mm, v(0.79, -12.66) * mm, v(-0.45, -12.11) * mm]});
            skFitSpline(sketch, "E274", {"points": [v(-0.45, -12.11) * mm, v(-1.7, -11.53) * mm, v(-2.74, -10.77) * mm, v(-3.6, -9.84) * mm]});
            skFitSpline(sketch, "E275", {"points": [v(-3.6, -9.84) * mm, v(-4.45, -8.87) * mm, v(-5.11, -7.73) * mm, v(-5.58, -6.4) * mm]});
            skFitSpline(sketch, "E276", {"points": [v(-5.58, -6.4) * mm, v(-6, -5.09) * mm, v(-6.22, -3.67) * mm, v(-6.22, -2.16) * mm]});
            skFitSpline(sketch, "E277", {"points": [v(-6.22, -1.4) * mm, v(-6.22, -1.01) * mm, v(-6.2, -0.72) * mm, v(-6.16, -0.53) * mm]});
            skFitSpline(sketch, "E278", {"points": [v(-6.16, -0.53) * mm, v(-4.88, -0.49) * mm, v(-3.62, -0.45) * mm, v(-2.37, -0.4) * mm]});
            skFitSpline(sketch, "E279", {"points": [v(-2.37, -0.4) * mm, v(-1.1, -0.37) * mm, v(0.19, -0.35) * mm, v(1.47, -0.35) * mm]});
            skFitSpline(sketch, "E280", {"points": [v(1.47, -0.35) * mm, v(3.56, -0.35) * mm, v(5.64, -0.37) * mm, v(7.7, -0.4) * mm]});
            skFitSpline(sketch, "E281", {"points": [v(7.7, -0.4) * mm, v(9.76, -0.45) * mm, v(11.83, -0.49) * mm, v(13.93, -0.53) * mm]});
            skFitSpline(sketch, "E282", {"points": [v(13.93, -0.53) * mm, v(13.97, -0.14) * mm, v(13.99, 0.23) * mm, v(13.99, 0.58) * mm]});
            skFitSpline(sketch, "E283", {"points": [v(13.99, 0.58) * mm, v(14.03, 0.97) * mm, v(14.05, 1.36) * mm, v(14.05, 1.74) * mm]});
            skFitSpline(sketch, "E284", {"points": [v(14.05, 1.74) * mm, v(14.05, 3.37) * mm, v(13.8, 4.9) * mm, v(13.29, 6.34) * mm]});
            skFitSpline(sketch, "E285", {"points": [v(13.29, 6.34) * mm, v(12.82, 7.78) * mm, v(12.09, 9.02) * mm, v(11.08, 10.07) * mm]});
            skFitSpline(sketch, "E286", {"points": [v(11.08, 10.07) * mm, v(10.07, 11.16) * mm, v(8.8, 12.01) * mm, v(7.3, 12.63) * mm]});
            skFitSpline(sketch, "E287", {"points": [v(7.3, 12.63) * mm, v(5.82, 13.3) * mm, v(4.05, 13.62) * mm, v(2, 13.62) * mm]});
            skFitSpline(sketch, "E288", {"points": [v(2, 13.62) * mm, v(-2.35, 13.62) * mm, v(-5.67, 12.26) * mm, v(-7.96, 9.55) * mm]});
            skFitSpline(sketch, "E289", {"points": [v(-7.96, 9.55) * mm, v(-10.21, 6.83) * mm, v(-11.34, 3.08) * mm, v(-11.34, -1.7) * mm]});
            skFitSpline(sketch, "E290", {"points": [v(20.22, 18.8) * mm, v(20.3, 17.56) * mm, v(20.34, 16.36) * mm, v(20.34, 15.2) * mm]});
            skFitSpline(sketch, "E291", {"points": [v(20.34, 15.2) * mm, v(20.38, 14.03) * mm, v(20.41, 13.06) * mm, v(20.45, 12.28) * mm]});
            skFitSpline(sketch, "E292", {"points": [v(20.45, 12.28) * mm, v(19.64, 12.28) * mm, v(18.36, 12.34) * mm, v(16.6, 12.46) * mm]});
            skFitSpline(sketch, "E293", {"points": [v(16.6, 12.46) * mm, v(16.65, 12.26) * mm, v(16.67, 12.07) * mm, v(16.67, 11.88) * mm]});
            skFitSpline(sketch, "E294", {"points": [v(16.67, 11.88) * mm, v(16.7, 11.68) * mm, v(16.73, 11.49) * mm, v(16.73, 11.3) * mm]});
            skFitSpline(sketch, "E295", {"points": [v(16.73, 11.3) * mm, v(16.73, 11.06) * mm, v(16.7, 10.83) * mm, v(16.67, 10.6) * mm]});
            skFitSpline(sketch, "E296", {"points": [v(16.67, 10.6) * mm, v(16.67, 10.4) * mm, v(16.65, 10.19) * mm, v(16.6, 9.95) * mm]});
            skFitSpline(sketch, "E297", {"points": [v(16.6, 9.95) * mm, v(17, 10) * mm, v(17.37, 10.01) * mm, v(17.72, 10.01) * mm]});
            skFitSpline(sketch, "E298", {"points": [v(17.72, 10.01) * mm, v(18.07, 10.05) * mm, v(18.4, 10.07) * mm, v(18.7, 10.07) * mm]});
            skFitSpline(sketch, "E299", {"points": [v(20.57, 10.07) * mm, v(20.57, 7.9) * mm, v(20.55, 5.92) * mm, v(20.51, 4.13) * mm]});
            skFitSpline(sketch, "E300", {"points": [v(20.51, 4.13) * mm, v(20.47, 2.39) * mm, v(20.41, 0.77) * mm, v(20.34, -0.7) * mm]});
            skFitSpline(sketch, "E301", {"points": [v(20.34, -0.7) * mm, v(20.3, -2.14) * mm, v(20.26, -3.48) * mm, v(20.22, -4.72) * mm]});
            skFitSpline(sketch, "E302", {"points": [v(20.22, -4.72) * mm, v(20.18, -5.92) * mm, v(20.16, -7.05) * mm, v(20.16, -8.1) * mm]});
            skFitSpline(sketch, "E303", {"points": [v(20.16, -8.1) * mm, v(20.16, -10.42) * mm, v(20.74, -12.2) * mm, v(21.9, -13.4) * mm]});
            skFitSpline(sketch, "E304", {"points": [v(21.9, -13.4) * mm, v(23.07, -14.6) * mm, v(24.88, -15.2) * mm, v(27.32, -15.2) * mm]});
            skFitSpline(sketch, "E305", {"points": [v(27.32, -15.2) * mm, v(28.06, -15.2) * mm, v(28.82, -15.1) * mm, v(29.6, -14.9) * mm]});
            skFitSpline(sketch, "E306", {"points": [v(29.6, -14.9) * mm, v(30.4, -14.75) * mm, v(31.15, -14.62) * mm, v(31.8, -14.5) * mm]});
            skFitSpline(sketch, "E307", {"points": [v(31.8, -13.1) * mm, v(31.42, -13.22) * mm, v(30.95, -13.32) * mm, v(30.4, -13.4) * mm]});
            skFitSpline(sketch, "E308", {"points": [v(30.4, -13.4) * mm, v(29.9, -13.47) * mm, v(29.5, -13.51) * mm, v(29.19, -13.51) * mm]});
            skFitSpline(sketch, "E309", {"points": [v(29.19, -13.51) * mm, v(28.02, -13.51) * mm, v(27.13, -13.26) * mm, v(26.5, -12.75) * mm]});
            skFitSpline(sketch, "E310", {"points": [v(26.5, -12.75) * mm, v(25.89, -12.25) * mm, v(25.42, -11.59) * mm, v(25.11, -10.77) * mm]});
            skFitSpline(sketch, "E311", {"points": [v(25.11, -10.77) * mm, v(24.8, -9.92) * mm, v(24.6, -8.97) * mm, v(24.53, -7.92) * mm]});
            skFitSpline(sketch, "E312", {"points": [v(24.53, -7.92) * mm, v(24.49, -6.87) * mm, v(24.47, -5.8) * mm, v(24.47, -4.72) * mm]});
            skFitSpline(sketch, "E313", {"points": [v(24.47, -4.72) * mm, v(24.47, -3.44) * mm, v(24.47, -1.98) * mm, v(24.47, -0.35) * mm]});
            skFitSpline(sketch, "E314", {"points": [v(24.47, -0.35) * mm, v(24.5, 1.28) * mm, v(24.55, 2.83) * mm, v(24.59, 4.3) * mm]});
            skFitSpline(sketch, "E315", {"points": [v(24.59, 4.3) * mm, v(24.63, 5.82) * mm, v(24.66, 7.12) * mm, v(24.7, 8.2) * mm]});
            skFitSpline(sketch, "E316", {"points": [v(24.7, 8.2) * mm, v(24.78, 9.3) * mm, v(24.84, 9.92) * mm, v(24.88, 10.07) * mm]});
            skFitSpline(sketch, "E317", {"points": [v(27.73, 10.07) * mm, v(28.35, 10.07) * mm, v(28.93, 10.05) * mm, v(29.48, 10.01) * mm]});
            skFitSpline(sketch, "E318", {"points": [v(29.48, 10.01) * mm, v(30.02, 10.01) * mm, v(30.54, 10) * mm, v(31.05, 9.95) * mm]});
            skFitSpline(sketch, "E319", {"points": [v(31.05, 9.95) * mm, v(31.01, 10.07) * mm, v(31, 10.26) * mm, v(31, 10.54) * mm]});
            skFitSpline(sketch, "E320", {"points": [v(31, 11.76) * mm, v(31, 12.07) * mm, v(31.01, 12.28) * mm, v(31.05, 12.4) * mm]});
            skFitSpline(sketch, "E321", {"points": [v(31.05, 12.4) * mm, v(29.7, 12.32) * mm, v(28.43, 12.26) * mm, v(27.26, 12.23) * mm]});
            skFitSpline(sketch, "E322", {"points": [v(27.26, 12.23) * mm, v(26.1, 12.23) * mm, v(25.3, 12.23) * mm, v(24.88, 12.23) * mm]});
            skFitSpline(sketch, "E323", {"points": [v(24.88, 12.23) * mm, v(24.96, 13.66) * mm, v(25.01, 15.08) * mm, v(25.05, 16.48) * mm]});
            skFitSpline(sketch, "E324", {"points": [v(25.05, 16.48) * mm, v(25.13, 17.91) * mm, v(25.23, 19.37) * mm, v(25.34, 20.84) * mm]});
            skFitSpline(sketch, "E325", {"points": [v(39.04, -0.88) * mm, v(39.04, 0.75) * mm, v(39.18, 2.33) * mm, v(39.45, 3.84) * mm]});
            skFitSpline(sketch, "E326", {"points": [v(39.45, 3.84) * mm, v(39.76, 5.35) * mm, v(40.27, 6.7) * mm, v(40.96, 7.86) * mm]});
            skFitSpline(sketch, "E327", {"points": [v(40.96, 7.86) * mm, v(41.66, 9.06) * mm, v(42.6, 10.01) * mm, v(43.76, 10.71) * mm]});
            skFitSpline(sketch, "E328", {"points": [v(43.76, 10.71) * mm, v(44.92, 11.4) * mm, v(46.36, 11.76) * mm, v(48.07, 11.76) * mm]});
            skFitSpline(sketch, "E329", {"points": [v(48.07, 11.76) * mm, v(49.78, 11.76) * mm, v(51.21, 11.4) * mm, v(52.38, 10.71) * mm]});
            skFitSpline(sketch, "E330", {"points": [v(52.38, 10.71) * mm, v(53.54, 10.01) * mm, v(54.47, 9.06) * mm, v(55.17, 7.86) * mm]});
            skFitSpline(sketch, "E331", {"points": [v(55.17, 7.86) * mm, v(55.87, 6.7) * mm, v(56.36, 5.35) * mm, v(56.63, 3.84) * mm]});
            skFitSpline(sketch, "E332", {"points": [v(56.63, 3.84) * mm, v(56.94, 2.33) * mm, v(57.1, 0.75) * mm, v(57.1, -0.88) * mm]});
            skFitSpline(sketch, "E333", {"points": [v(57.1, -0.88) * mm, v(57.1, -2.5) * mm, v(56.94, -4.08) * mm, v(56.63, -5.6) * mm]});
            skFitSpline(sketch, "E334", {"points": [v(56.63, -5.6) * mm, v(56.36, -7.1) * mm, v(55.87, -8.46) * mm, v(55.17, -9.67) * mm]});
            skFitSpline(sketch, "E335", {"points": [v(55.17, -9.67) * mm, v(54.47, -10.83) * mm, v(53.54, -11.76) * mm, v(52.38, -12.46) * mm]});
            skFitSpline(sketch, "E336", {"points": [v(52.38, -12.46) * mm, v(51.21, -13.16) * mm, v(49.78, -13.51) * mm, v(48.07, -13.51) * mm]});
            skFitSpline(sketch, "E337", {"points": [v(48.07, -13.51) * mm, v(46.36, -13.51) * mm, v(44.92, -13.16) * mm, v(43.76, -12.46) * mm]});
            skFitSpline(sketch, "E338", {"points": [v(43.76, -12.46) * mm, v(42.6, -11.76) * mm, v(41.66, -10.83) * mm, v(40.96, -9.67) * mm]});
            skFitSpline(sketch, "E339", {"points": [v(40.96, -9.67) * mm, v(40.27, -8.46) * mm, v(39.76, -7.1) * mm, v(39.45, -5.6) * mm]});
            skFitSpline(sketch, "E340", {"points": [v(39.45, -5.6) * mm, v(39.18, -4.08) * mm, v(39.04, -2.5) * mm, v(39.04, -0.88) * mm]});
            skFitSpline(sketch, "E341", {"points": [v(33.92, -0.88) * mm, v(33.92, -3.51) * mm, v(34.33, -5.77) * mm, v(35.14, -7.63) * mm]});
            skFitSpline(sketch, "E342", {"points": [v(35.14, -7.63) * mm, v(36, -9.45) * mm, v(37.1, -10.95) * mm, v(38.46, -12.11) * mm]});
            skFitSpline(sketch, "E343", {"points": [v(38.46, -12.11) * mm, v(39.82, -13.24) * mm, v(41.33, -14.03) * mm, v(43, -14.5) * mm]});
            skFitSpline(sketch, "E344", {"points": [v(43, -14.5) * mm, v(44.71, -14.97) * mm, v(46.4, -15.2) * mm, v(48.07, -15.2) * mm]});
            skFitSpline(sketch, "E345", {"points": [v(48.07, -15.2) * mm, v(49.78, -15.2) * mm, v(51.46, -14.97) * mm, v(53.13, -14.5) * mm]});
            skFitSpline(sketch, "E346", {"points": [v(53.13, -14.5) * mm, v(54.8, -14.03) * mm, v(56.32, -13.24) * mm, v(57.68, -12.11) * mm]});
            skFitSpline(sketch, "E347", {"points": [v(57.68, -12.11) * mm, v(59.03, -10.95) * mm, v(60.12, -9.45) * mm, v(60.94, -7.63) * mm]});
            skFitSpline(sketch, "E348", {"points": [v(60.94, -7.63) * mm, v(61.79, -5.77) * mm, v(62.22, -3.51) * mm, v(62.22, -0.88) * mm]});
            skFitSpline(sketch, "E349", {"points": [v(62.22, -0.88) * mm, v(62.22, 1.76) * mm, v(61.79, 4) * mm, v(60.94, 5.82) * mm]});
            skFitSpline(sketch, "E350", {"points": [v(60.94, 5.82) * mm, v(60.12, 7.68) * mm, v(59.03, 9.18) * mm, v(57.68, 10.3) * mm]});
            skFitSpline(sketch, "E351", {"points": [v(57.68, 10.3) * mm, v(56.32, 11.47) * mm, v(54.8, 12.3) * mm, v(53.13, 12.8) * mm]});
            skFitSpline(sketch, "E352", {"points": [v(53.13, 12.8) * mm, v(51.46, 13.35) * mm, v(49.78, 13.62) * mm, v(48.07, 13.62) * mm]});
            skFitSpline(sketch, "E353", {"points": [v(48.07, 13.62) * mm, v(46.4, 13.62) * mm, v(44.71, 13.35) * mm, v(43, 12.8) * mm]});
            skFitSpline(sketch, "E354", {"points": [v(43, 12.8) * mm, v(41.33, 12.3) * mm, v(39.82, 11.47) * mm, v(38.46, 10.3) * mm]});
            skFitSpline(sketch, "E355", {"points": [v(38.46, 10.3) * mm, v(37.1, 9.18) * mm, v(36, 7.68) * mm, v(35.14, 5.82) * mm]});
            skFitSpline(sketch, "E356", {"points": [v(35.14, 5.82) * mm, v(34.33, 4) * mm, v(33.92, 1.76) * mm, v(33.92, -0.88) * mm]});
            skFitSpline(sketch, "E357", {"points": [v(-39.4, -54.15) * mm, v(-39.4, -52.4) * mm, v(-39.25, -50.77) * mm, v(-38.94, -49.26) * mm]});
            skFitSpline(sketch, "E358", {"points": [v(-38.94, -49.26) * mm, v(-38.6, -47.7) * mm, v(-38.09, -46.36) * mm, v(-37.43, -45.24) * mm]});
            skFitSpline(sketch, "E359", {"points": [v(-37.43, -45.24) * mm, v(-36.73, -44.07) * mm, v(-35.87, -43.18) * mm, v(-34.87, -42.56) * mm]});
            skFitSpline(sketch, "E360", {"points": [v(-34.87, -42.56) * mm, v(-33.82, -41.9) * mm, v(-32.6, -41.57) * mm, v(-31.2, -41.57) * mm]});
            skFitSpline(sketch, "E361", {"points": [v(-31.2, -41.57) * mm, v(-28.4, -41.57) * mm, v(-26.29, -42.56) * mm, v(-24.85, -44.54) * mm]});
            skFitSpline(sketch, "E362", {"points": [v(-24.85, -44.54) * mm, v(-23.41, -46.48) * mm, v(-22.7, -49.31) * mm, v(-22.7, -53.04) * mm]});
            skFitSpline(sketch, "E363", {"points": [v(-22.7, -53.04) * mm, v(-22.7, -54.6) * mm, v(-22.87, -56.15) * mm, v(-23.22, -57.7) * mm]});
            skFitSpline(sketch, "E364", {"points": [v(-23.22, -57.7) * mm, v(-23.53, -59.25) * mm, v(-24.06, -60.65) * mm, v(-24.8, -61.9) * mm]});
            skFitSpline(sketch, "E365", {"points": [v(-24.8, -61.9) * mm, v(-25.5, -63.1) * mm, v(-26.38, -64.08) * mm, v(-27.47, -64.86) * mm]});
            skFitSpline(sketch, "E366", {"points": [v(-27.47, -64.86) * mm, v(-28.56, -65.6) * mm, v(-29.86, -65.97) * mm, v(-31.37, -65.97) * mm]});
            skFitSpline(sketch, "E367", {"points": [v(-31.37, -65.97) * mm, v(-32.3, -65.97) * mm, v(-33.25, -65.8) * mm, v(-34.22, -65.44) * mm]});
            skFitSpline(sketch, "E368", {"points": [v(-34.22, -65.44) * mm, v(-35.2, -65.1) * mm, v(-36.07, -64.47) * mm, v(-36.84, -63.58) * mm]});
            skFitSpline(sketch, "E369", {"points": [v(-36.84, -63.58) * mm, v(-37.58, -62.65) * mm, v(-38.2, -61.42) * mm, v(-38.7, -59.91) * mm]});
            skFitSpline(sketch, "E370", {"points": [v(-38.7, -59.91) * mm, v(-39.17, -58.4) * mm, v(-39.4, -56.48) * mm, v(-39.4, -54.15) * mm]});
            skFitSpline(sketch, "E371", {"points": [v(-22.93, -67.36) * mm, v(-22.15, -67.29) * mm, v(-21.42, -67.25) * mm, v(-20.72, -67.25) * mm]});
            skFitSpline(sketch, "E372", {"points": [v(-20.72, -67.25) * mm, v(-19.98, -67.25) * mm, v(-19.22, -67.29) * mm, v(-18.45, -67.36) * mm]});
            skFitSpline(sketch, "E373", {"points": [v(-18.45, -67.36) * mm, v(-18.48, -65.11) * mm, v(-18.52, -62.92) * mm, v(-18.56, -60.78) * mm]});
            skFitSpline(sketch, "E374", {"points": [v(-18.56, -60.78) * mm, v(-18.6, -58.65) * mm, v(-18.62, -56.24) * mm, v(-18.62, -53.56) * mm]});
            skFitSpline(sketch, "E375", {"points": [v(-18.62, -53.56) * mm, v(-18.62, -51.08) * mm, v(-18.6, -48.34) * mm, v(-18.56, -45.35) * mm]});
            skFitSpline(sketch, "E376", {"points": [v(-18.56, -45.35) * mm, v(-18.52, -42.37) * mm, v(-18.48, -39.45) * mm, v(-18.45, -36.62) * mm]});
            skFitSpline(sketch, "E377", {"points": [v(-18.45, -36.62) * mm, v(-18.37, -33.79) * mm, v(-18.3, -31.2) * mm, v(-18.21, -28.88) * mm]});
            skFitSpline(sketch, "E378", {"points": [v(-18.21, -28.88) * mm, v(-18.14, -26.5) * mm, v(-18.04, -24.7) * mm, v(-17.92, -23.46) * mm]});
            skFitSpline(sketch, "E379", {"points": [v(-17.92, -23.46) * mm, v(-18.43, -23.54) * mm, v(-18.9, -23.62) * mm, v(-19.32, -23.7) * mm]});
            skFitSpline(sketch, "E380", {"points": [v(-19.32, -23.7) * mm, v(-19.7, -23.73) * mm, v(-20.12, -23.75) * mm, v(-20.54, -23.75) * mm]});
            skFitSpline(sketch, "E381", {"points": [v(-20.54, -23.75) * mm, v(-20.97, -23.75) * mm, v(-21.4, -23.73) * mm, v(-21.82, -23.7) * mm]});
            skFitSpline(sketch, "E382", {"points": [v(-21.82, -23.7) * mm, v(-22.25, -23.62) * mm, v(-22.7, -23.54) * mm, v(-23.16, -23.46) * mm]});
            skFitSpline(sketch, "E383", {"points": [v(-23.16, -23.46) * mm, v(-23.12, -24.4) * mm, v(-23.1, -25.46) * mm, v(-23.1, -26.66) * mm]});
            skFitSpline(sketch, "E384", {"points": [v(-23.1, -26.66) * mm, v(-23.07, -27.87) * mm, v(-23.05, -29.15) * mm, v(-23.05, -30.5) * mm]});
            skFitSpline(sketch, "E385", {"points": [v(-23.05, -30.5) * mm, v(-23, -31.87) * mm, v(-22.99, -33.3) * mm, v(-22.99, -34.82) * mm]});
            skFitSpline(sketch, "E386", {"points": [v(-22.99, -34.82) * mm, v(-22.95, -36.3) * mm, v(-22.93, -37.77) * mm, v(-22.93, -39.24) * mm]});
            skFitSpline(sketch, "E387", {"points": [v(-23.05, -44.95) * mm, v(-24.71, -41.07) * mm, v(-27.7, -39.12) * mm, v(-32.01, -39.12) * mm]});
            skFitSpline(sketch, "E388", {"points": [v(-32.01, -39.12) * mm, v(-33.53, -39.12) * mm, v(-35.04, -39.43) * mm, v(-36.55, -40.06) * mm]});
            skFitSpline(sketch, "E389", {"points": [v(-36.55, -40.06) * mm, v(-38.03, -40.64) * mm, v(-39.37, -41.55) * mm, v(-40.57, -42.8) * mm]});
            skFitSpline(sketch, "E390", {"points": [v(-40.57, -42.8) * mm, v(-41.74, -44) * mm, v(-42.69, -45.5) * mm, v(-43.42, -47.33) * mm]});
            skFitSpline(sketch, "E391", {"points": [v(-43.42, -47.33) * mm, v(-44.16, -49.16) * mm, v(-44.53, -51.31) * mm, v(-44.53, -53.8) * mm]});
            skFitSpline(sketch, "E392", {"points": [v(-44.53, -53.8) * mm, v(-44.53, -56.32) * mm, v(-44.2, -58.5) * mm, v(-43.54, -60.32) * mm]});
            skFitSpline(sketch, "E393", {"points": [v(-43.54, -60.32) * mm, v(-42.84, -62.1) * mm, v(-41.95, -63.58) * mm, v(-40.86, -64.74) * mm]});
            skFitSpline(sketch, "E394", {"points": [v(-40.86, -64.74) * mm, v(-39.74, -65.87) * mm, v(-38.48, -66.68) * mm, v(-37.08, -67.19) * mm]});
            skFitSpline(sketch, "E395", {"points": [v(-37.08, -67.19) * mm, v(-35.64, -67.7) * mm, v(-34.19, -67.95) * mm, v(-32.71, -67.95) * mm]});
            skFitSpline(sketch, "E396", {"points": [v(-32.71, -67.95) * mm, v(-31.27, -67.95) * mm, v(-30.01, -67.75) * mm, v(-28.93, -67.36) * mm]});
            skFitSpline(sketch, "E397", {"points": [v(-28.93, -67.36) * mm, v(-27.84, -66.97) * mm, v(-26.9, -66.47) * mm, v(-26.13, -65.85) * mm]});
            skFitSpline(sketch, "E398", {"points": [v(-26.13, -65.85) * mm, v(-25.32, -65.23) * mm, v(-24.66, -64.57) * mm, v(-24.15, -63.87) * mm]});
            skFitSpline(sketch, "E399", {"points": [v(-24.15, -63.87) * mm, v(-23.6, -63.13) * mm, v(-23.18, -62.45) * mm, v(-22.87, -61.83) * mm]});
            skFitSpline(sketch, "E400", {"points": [v(0.8, -40.99) * mm, v(2.32, -40.99) * mm, v(3.54, -41.32) * mm, v(4.48, -41.98) * mm]});
            skFitSpline(sketch, "E401", {"points": [v(4.48, -41.98) * mm, v(5.4, -42.64) * mm, v(6.13, -43.47) * mm, v(6.63, -44.48) * mm]});
            skFitSpline(sketch, "E402", {"points": [v(6.63, -44.48) * mm, v(7.17, -45.5) * mm, v(7.52, -46.58) * mm, v(7.68, -47.74) * mm]});
            skFitSpline(sketch, "E403", {"points": [v(7.68, -47.74) * mm, v(7.87, -48.9) * mm, v(7.97, -50.01) * mm, v(7.97, -51.06) * mm]});
            skFitSpline(sketch, "E404", {"points": [v(7.97, -51.06) * mm, v(6.73, -51.1) * mm, v(5.45, -51.14) * mm, v(4.13, -51.18) * mm]});
            skFitSpline(sketch, "E405", {"points": [v(4.13, -51.18) * mm, v(2.8, -51.22) * mm, v(1.5, -51.24) * mm, v(0.23, -51.24) * mm]});
            skFitSpline(sketch, "E406", {"points": [v(0.23, -51.24) * mm, v(-1.02, -51.24) * mm, v(-2.3, -51.22) * mm, v(-3.62, -51.18) * mm]});
            skFitSpline(sketch, "E407", {"points": [v(-3.62, -51.18) * mm, v(-4.9, -51.14) * mm, v(-6.14, -51.1) * mm, v(-7.34, -51.06) * mm]});
            skFitSpline(sketch, "E408", {"points": [v(-7.34, -51.06) * mm, v(-7.27, -50.01) * mm, v(-7.07, -48.9) * mm, v(-6.76, -47.74) * mm]});
            skFitSpline(sketch, "E409", {"points": [v(-6.76, -47.74) * mm, v(-6.41, -46.54) * mm, v(-5.93, -45.45) * mm, v(-5.3, -44.48) * mm]});
            skFitSpline(sketch, "E410", {"points": [v(-5.3, -44.48) * mm, v(-4.65, -43.47) * mm, v(-3.83, -42.64) * mm, v(-2.86, -41.98) * mm]});
            skFitSpline(sketch, "E411", {"points": [v(-2.86, -41.98) * mm, v(-1.85, -41.32) * mm, v(-0.63, -40.99) * mm, v(0.8, -40.99) * mm]});
            skFitSpline(sketch, "E412", {"points": [v(-12.64, -54.44) * mm, v(-12.64, -56.38) * mm, v(-12.31, -58.18) * mm, v(-11.65, -59.85) * mm]});
            skFitSpline(sketch, "E413", {"points": [v(-11.65, -59.85) * mm, v(-10.95, -61.52) * mm, v(-9.98, -62.98) * mm, v(-8.74, -64.22) * mm]});
            skFitSpline(sketch, "E414", {"points": [v(-8.74, -64.22) * mm, v(-7.46, -65.42) * mm, v(-5.97, -66.35) * mm, v(-4.26, -67.01) * mm]});
            skFitSpline(sketch, "E415", {"points": [v(-4.26, -67.01) * mm, v(-2.51, -67.63) * mm, v(-0.59, -67.95) * mm, v(1.5, -67.95) * mm]});
            skFitSpline(sketch, "E416", {"points": [v(1.5, -67.95) * mm, v(3.37, -67.95) * mm, v(5.16, -67.62) * mm, v(6.86, -66.96) * mm]});
            skFitSpline(sketch, "E417", {"points": [v(6.86, -66.96) * mm, v(8.6, -66.3) * mm, v(10.07, -65.5) * mm, v(11.23, -64.57) * mm]});
            skFitSpline(sketch, "E418", {"points": [v(11.29, -61.54) * mm, v(10.78, -62.12) * mm, v(10.18, -62.67) * mm, v(9.48, -63.17) * mm]});
            skFitSpline(sketch, "E419", {"points": [v(9.48, -63.17) * mm, v(8.82, -63.68) * mm, v(8.1, -64.12) * mm, v(7.33, -64.51) * mm]});
            skFitSpline(sketch, "E420", {"points": [v(7.33, -64.51) * mm, v(6.55, -64.86) * mm, v(5.76, -65.15) * mm, v(4.94, -65.38) * mm]});
            skFitSpline(sketch, "E421", {"points": [v(4.94, -65.38) * mm, v(4.13, -65.58) * mm, v(3.33, -65.67) * mm, v(2.55, -65.67) * mm]});
            skFitSpline(sketch, "E422", {"points": [v(2.55, -65.67) * mm, v(0.92, -65.67) * mm, v(-0.51, -65.4) * mm, v(-1.75, -64.86) * mm]});
            skFitSpline(sketch, "E423", {"points": [v(-1.75, -64.86) * mm, v(-3, -64.28) * mm, v(-4.04, -63.52) * mm, v(-4.9, -62.59) * mm]});
            skFitSpline(sketch, "E424", {"points": [v(-4.9, -62.59) * mm, v(-5.75, -61.62) * mm, v(-6.41, -60.47) * mm, v(-6.88, -59.15) * mm]});
            skFitSpline(sketch, "E425", {"points": [v(-6.88, -59.15) * mm, v(-7.3, -57.83) * mm, v(-7.52, -56.42) * mm, v(-7.52, -54.9) * mm]});
            skFitSpline(sketch, "E426", {"points": [v(-7.52, -54.15) * mm, v(-7.52, -53.76) * mm, v(-7.5, -53.47) * mm, v(-7.46, -53.27) * mm]});
            skFitSpline(sketch, "E427", {"points": [v(-7.46, -53.27) * mm, v(-6.18, -53.23) * mm, v(-4.92, -53.2) * mm, v(-3.68, -53.16) * mm]});
            skFitSpline(sketch, "E428", {"points": [v(-3.68, -53.16) * mm, v(-2.4, -53.12) * mm, v(-1.11, -53.1) * mm, v(0.17, -53.1) * mm]});
            skFitSpline(sketch, "E429", {"points": [v(0.17, -53.1) * mm, v(2.26, -53.1) * mm, v(4.34, -53.12) * mm, v(6.4, -53.16) * mm]});
            skFitSpline(sketch, "E430", {"points": [v(6.4, -53.16) * mm, v(8.45, -53.2) * mm, v(10.53, -53.23) * mm, v(12.63, -53.27) * mm]});
            skFitSpline(sketch, "E431", {"points": [v(12.63, -53.27) * mm, v(12.67, -52.88) * mm, v(12.69, -52.52) * mm, v(12.69, -52.17) * mm]});
            skFitSpline(sketch, "E432", {"points": [v(12.69, -52.17) * mm, v(12.72, -51.78) * mm, v(12.74, -51.4) * mm, v(12.74, -51) * mm]});
            skFitSpline(sketch, "E433", {"points": [v(12.74, -51) * mm, v(12.74, -49.37) * mm, v(12.5, -47.84) * mm, v(11.99, -46.4) * mm]});
            skFitSpline(sketch, "E434", {"points": [v(11.99, -46.4) * mm, v(11.52, -44.97) * mm, v(10.78, -43.72) * mm, v(9.77, -42.68) * mm]});
            skFitSpline(sketch, "E435", {"points": [v(9.77, -42.68) * mm, v(8.77, -41.59) * mm, v(7.5, -40.74) * mm, v(5.99, -40.11) * mm]});
            skFitSpline(sketch, "E436", {"points": [v(5.99, -40.11) * mm, v(4.51, -39.45) * mm, v(2.75, -39.12) * mm, v(0.7, -39.12) * mm]});
            skFitSpline(sketch, "E437", {"points": [v(0.7, -39.12) * mm, v(-3.66, -39.12) * mm, v(-6.97, -40.48) * mm, v(-9.26, -43.2) * mm]});
            skFitSpline(sketch, "E438", {"points": [v(-9.26, -43.2) * mm, v(-11.52, -45.92) * mm, v(-12.64, -49.66) * mm, v(-12.64, -54.44) * mm]});
            skFitSpline(sketch, "E439", {"points": [v(37.72, -54.55) * mm, v(37.72, -56.8) * mm, v(37.67, -59) * mm, v(37.55, -61.13) * mm]});
            skFitSpline(sketch, "E440", {"points": [v(37.55, -61.13) * mm, v(37.47, -63.27) * mm, v(37.4, -65.34) * mm, v(37.32, -67.36) * mm]});
            skFitSpline(sketch, "E441", {"points": [v(37.32, -67.36) * mm, v(38.1, -67.29) * mm, v(38.89, -67.25) * mm, v(39.7, -67.25) * mm]});
            skFitSpline(sketch, "E442", {"points": [v(39.7, -67.25) * mm, v(40.56, -67.25) * mm, v(41.37, -67.29) * mm, v(42.15, -67.36) * mm]});
            skFitSpline(sketch, "E443", {"points": [v(42.15, -67.36) * mm, v(42.11, -66.82) * mm, v(42.07, -66.26) * mm, v(42.03, -65.67) * mm]});
            skFitSpline(sketch, "E444", {"points": [v(42.03, -65.67) * mm, v(42.03, -65.05) * mm, v(42.03, -64.43) * mm, v(42.03, -63.81) * mm]});
            skFitSpline(sketch, "E445", {"points": [v(42.03, -60.03) * mm, v(42.03, -58.05) * mm, v(42.07, -56.18) * mm, v(42.15, -54.44) * mm]});
            skFitSpline(sketch, "E446", {"points": [v(42.15, -54.44) * mm, v(42.23, -52.65) * mm, v(42.27, -50.92) * mm, v(42.27, -49.26) * mm]});
            skFitSpline(sketch, "E447", {"points": [v(42.27, -49.26) * mm, v(42.27, -47.24) * mm, v(41.98, -45.59) * mm, v(41.4, -44.3) * mm]});
            skFitSpline(sketch, "E448", {"points": [v(41.4, -44.3) * mm, v(40.85, -42.99) * mm, v(40.13, -41.96) * mm, v(39.24, -41.22) * mm]});
            skFitSpline(sketch, "E449", {"points": [v(39.24, -41.22) * mm, v(38.35, -40.44) * mm, v(37.34, -39.9) * mm, v(36.21, -39.6) * mm]});
            skFitSpline(sketch, "E450", {"points": [v(36.21, -39.6) * mm, v(35.12, -39.28) * mm, v(34.04, -39.12) * mm, v(32.95, -39.12) * mm]});
            skFitSpline(sketch, "E451", {"points": [v(32.95, -39.12) * mm, v(30.85, -39.12) * mm, v(29.05, -39.6) * mm, v(27.54, -40.52) * mm]});
            skFitSpline(sketch, "E452", {"points": [v(27.54, -40.52) * mm, v(26.02, -41.41) * mm, v(24.72, -42.7) * mm, v(23.63, -44.36) * mm]});
            skFitSpline(sketch, "E453", {"points": [v(23.52, -44.36) * mm, v(23.52, -42.81) * mm, v(23.58, -41.26) * mm, v(23.7, -39.7) * mm]});
            skFitSpline(sketch, "E454", {"points": [v(23.7, -39.7) * mm, v(23.19, -39.78) * mm, v(22.74, -39.86) * mm, v(22.35, -39.94) * mm]});
            skFitSpline(sketch, "E455", {"points": [v(22.35, -39.94) * mm, v(22, -39.98) * mm, v(21.67, -40) * mm, v(21.36, -40) * mm]});
            skFitSpline(sketch, "E456", {"points": [v(21.36, -40) * mm, v(20.7, -40) * mm, v(19.83, -39.9) * mm, v(18.74, -39.7) * mm]});
            skFitSpline(sketch, "E457", {"points": [v(18.74, -39.7) * mm, v(18.94, -41.38) * mm, v(19.05, -43.18) * mm, v(19.1, -45.12) * mm]});
            skFitSpline(sketch, "E458", {"points": [v(19.1, -45.12) * mm, v(19.17, -47.02) * mm, v(19.2, -48.85) * mm, v(19.2, -50.6) * mm]});
            skFitSpline(sketch, "E459", {"points": [v(19.2, -56.65) * mm, v(19.2, -58.4) * mm, v(19.17, -60.24) * mm, v(19.1, -62.18) * mm]});
            skFitSpline(sketch, "E460", {"points": [v(19.1, -62.18) * mm, v(19.05, -64.08) * mm, v(18.94, -65.81) * mm, v(18.74, -67.36) * mm]});
            skFitSpline(sketch, "E461", {"points": [v(18.74, -67.36) * mm, v(19.64, -67.29) * mm, v(20.5, -67.25) * mm, v(21.36, -67.25) * mm]});
            skFitSpline(sketch, "E462", {"points": [v(21.36, -67.25) * mm, v(22.22, -67.25) * mm, v(23.1, -67.29) * mm, v(23.98, -67.36) * mm]});
            skFitSpline(sketch, "E463", {"points": [v(23.98, -67.36) * mm, v(23.79, -65.81) * mm, v(23.65, -64.08) * mm, v(23.58, -62.18) * mm]});
            skFitSpline(sketch, "E464", {"points": [v(23.58, -62.18) * mm, v(23.54, -60.24) * mm, v(23.52, -58.4) * mm, v(23.52, -56.65) * mm]});
            skFitSpline(sketch, "E465", {"points": [v(23.52, -51.7) * mm, v(23.52, -48.67) * mm, v(24.14, -46.32) * mm, v(25.38, -44.66) * mm]});
            skFitSpline(sketch, "E466", {"points": [v(25.38, -44.66) * mm, v(26.66, -42.99) * mm, v(28.66, -42.15) * mm, v(31.38, -42.15) * mm]});
            skFitSpline(sketch, "E467", {"points": [v(31.38, -42.15) * mm, v(33.36, -42.15) * mm, v(34.91, -42.9) * mm, v(36.04, -44.42) * mm]});
            skFitSpline(sketch, "E468", {"points": [v(36.04, -44.42) * mm, v(37.16, -45.9) * mm, v(37.72, -48.1) * mm, v(37.72, -51) * mm]});
            skSolve(sketch);
        }
        {
            var Q0;
            Q0=makeQuery(id+"F0.imprint","IMPRINT",FACE,{"disambiguationData":[TD([[makeQuery(id+"F0.imprint","IMPRINT",EDGE,{"derivedFrom":sQuery(id+"F0.wireOp",EDGE,"E1")}),-1.0]])]});
            var Q1;
            Q1=makeQuery(id+"F0.imprint","IMPRINT",FACE,{"disambiguationData":[TD([[makeQuery(id+"F0.imprint","IMPRINT",EDGE,{"derivedFrom":sQuery(id+"F0.wireOp",EDGE,"E105")}),1.0]])]});
            var Q2;
            Q2=makeQuery(id+"F0.imprint","IMPRINT",FACE,{"disambiguationData":[TD([[makeQuery(id+"F0.imprint","IMPRINT",EDGE,{"derivedFrom":sQuery(id+"F0.wireOp",EDGE,"E5")}),-1.0]])]});
            var Q3;
            Q3=makeQuery(id+"F0.imprint","IMPRINT",FACE,{"disambiguationData":[TD([[makeQuery(id+"F0.imprint","IMPRINT",EDGE,{"derivedFrom":sQuery(id+"F0.wireOp",EDGE,"E13")}),-1.0]])]});
            var Q4;
            Q4=makeQuery(id+"F0.imprint","IMPRINT",FACE,{"disambiguationData":[TD([[makeQuery(id+"F0.imprint","IMPRINT",EDGE,{"derivedFrom":sQuery(id+"F0.wireOp",EDGE,"E23")}),-1.0]])]});
            var Q5;
            Q5=makeQuery(id+"F0.imprint","IMPRINT",FACE,{"disambiguationData":[TD([[makeQuery(id+"F0.imprint","IMPRINT",EDGE,{"derivedFrom":sQuery(id+"F0.wireOp",EDGE,"E32")}),-1.0]])]});
            var Q6;
            Q6=makeQuery(id+"F0.imprint","IMPRINT",FACE,{"disambiguationData":[TD([[makeQuery(id+"F0.imprint","IMPRINT",EDGE,{"derivedFrom":sQuery(id+"F0.wireOp",EDGE,"E36")}),-1.0]])]});
            var Q7;
            Q7=makeQuery(id+"F0.imprint","IMPRINT",FACE,{"disambiguationData":[TD([[makeQuery(id+"F0.imprint","IMPRINT",EDGE,{"derivedFrom":sQuery(id+"F0.wireOp",EDGE,"E325")}),1.0]])]});
            var Q8;
            Q8=makeQuery(id+"F0.imprint","IMPRINT",FACE,{"disambiguationData":[TD([[makeQuery(id+"F0.imprint","IMPRINT",EDGE,{"derivedFrom":sQuery(id+"F0.wireOp",EDGE,"E49")}),-1.0]])]});
            var Q9;
            Q9=makeQuery(id+"F0.imprint","IMPRINT",FACE,{"disambiguationData":[TD([[makeQuery(id+"F0.imprint","IMPRINT",EDGE,{"derivedFrom":sQuery(id+"F0.wireOp",EDGE,"E57")}),-1.0]])]});
            var Q10;
            Q10=makeQuery(id+"F0.imprint","IMPRINT",FACE,{"disambiguationData":[TD([[makeQuery(id+"F0.imprint","IMPRINT",EDGE,{"derivedFrom":sQuery(id+"F0.wireOp",EDGE,"E61")}),-1.0]])]});
            extrude(context, id + "F1", {"entities" : qUnion([Q0, Q1, Q2, Q3, Q4, Q5, Q6, Q7, Q8, Q9, Q10]), "depth" : 2 * mm, "offsetDistance" : 25 * mm});
        }
    });
